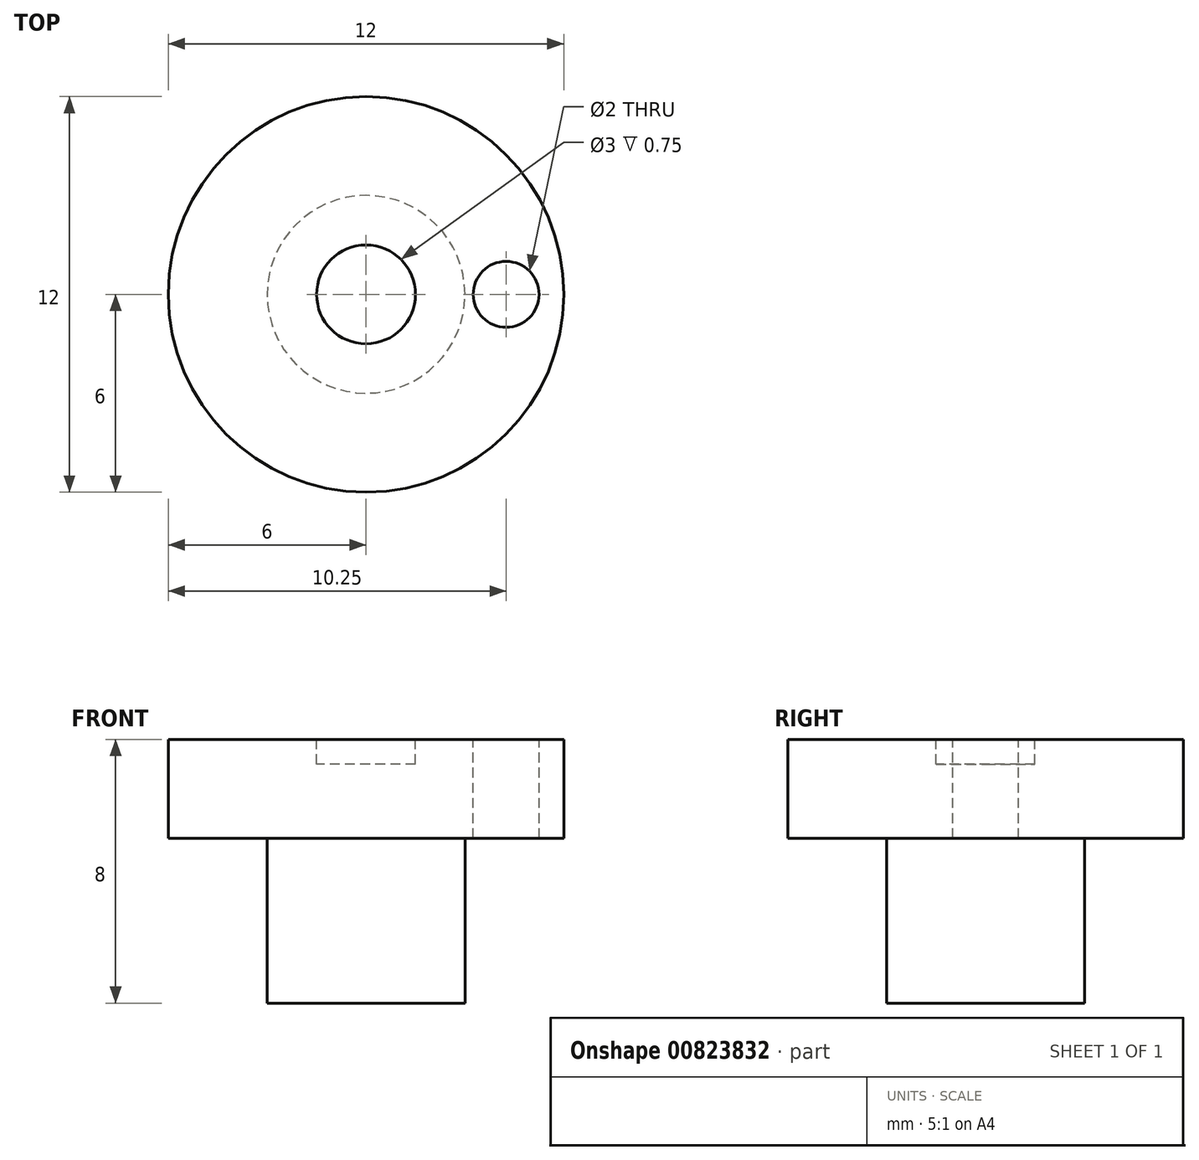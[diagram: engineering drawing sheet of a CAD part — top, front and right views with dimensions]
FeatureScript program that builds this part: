
annotation { "Feature Type Name" : "Feature", "Feature Type Description" : "" }
export const myFeature = defineFeature(function(context is Context, id is Id, definition is map)
    precondition{}
    {
        {
            var Q0;
            Q0=qCreatedBy(makeId("Front.planeOp"),FACE);
            var sketch = newSketch(context, id + "F0", { "sketchPlane" : qUnion([Q0])});
            skLineSegment(sketch, "E0", {"start": v(0, 0) * mm, "end": v(3, 0) * mm});
            skLineSegment(sketch, "E1", {"start": v(3, 0) * mm, "end": v(3, 5) * mm});
            skLineSegment(sketch, "E2", {"start": v(3, 5) * mm, "end": v(6, 5) * mm});
            skLineSegment(sketch, "E3", {"start": v(6, 5) * mm, "end": v(6, 8) * mm});
            skLineSegment(sketch, "E4", {"start": v(6, 8) * mm, "end": v(0, 8) * mm});
            skLineSegment(sketch, "E5", {"start": v(0, 8) * mm, "end": v(0, 0) * mm});
            skSolve(sketch);
        }
        {
            var Q0;
            Q0 = qSketchRegion(id + "F0", true);
            var Q1;
            Q1=sQuery(id+"F0.wireOp",EDGE,"E5");
            revolve(context, id + "F1", {"surfaceOperationType" : NewSurfaceOperationType.NEW, "entities" : qUnion([Q0]), "axis" : qUnion([Q1]), "revolveType" : RevolveType.FULL});
        }
        {
            var Q0;
            Q0=makeQuery(id+"F1.opRevolve","SWEPT_FACE",FACE,{"disambiguationData":[OSD([sQuery(id+"F0.wireOp",EDGE,"E4")])]});
            var sketch = newSketch(context, id + "F2", { "sketchPlane" : qUnion([Q0])});
            skCircle(sketch, "E6", {"center": v(0, 0) * mm, "radius": 4.25 * mm, "construction": true});
            skCircle(sketch, "E7", {"center": v(4.25, 0) * mm, "radius": 1 * mm});
            skSolve(sketch);
        }
        {
            var Q0;
            Q0=makeQuery(id+"F2.imprint","IMPRINT",FACE,{"disambiguationData":[TD([[makeQuery(id+"F2.imprint","IMPRINT",EDGE,{"derivedFrom":sQuery(id+"F2.wireOp",EDGE,"E7")}),1.0]])]});
            var Q1;
            Q1=sQuery(id+"F2.wireOp",EDGE,"E7");
            extrude(context, id + "F3", {"entities" : qUnion([Q0]), "operationType" : NewBodyOperationType.REMOVE, "surfaceEntities" : qUnion([Q1]), "endBound" : BoundingType.UP_TO_NEXT, "oppositeDirection" : true, "depth" : 25 * mm, "offsetDistance" : 25 * mm});
        }
        {
            var Q0;
            Q0=makeQuery(id+"F2.imprint","IMPRINT",FACE,{"disambiguationData":[TD([[makeQuery(id+"F2.imprint","IMPRINT",EDGE,{"derivedFrom":sQuery(id+"F2.wireOp",EDGE,"E7")}),-1.0]])]});
            var sketch = newSketch(context, id + "F4", { "sketchPlane" : qUnion([Q0])});
            skCircle(sketch, "E8", {"center": v(0, 0) * mm, "radius": 1.5 * mm});
            skSolve(sketch);
        }
        {
            var Q0;
            Q0=makeQuery(id+"F4.imprint","IMPRINT",FACE,{"disambiguationData":[TD([[makeQuery(id+"F4.imprint","IMPRINT",EDGE,{"derivedFrom":sQuery(id+"F4.wireOp",EDGE,"E8")}),1.0]])]});
            var Q1;
            Q1=sQuery(id+"F4.wireOp",EDGE,"E8");
            extrude(context, id + "F5", {"entities" : qUnion([Q0]), "operationType" : NewBodyOperationType.REMOVE, "surfaceEntities" : qUnion([Q1]), "oppositeDirection" : true, "depth" : .75 * mm, "offsetDistance" : 25 * mm});
        }
    });
